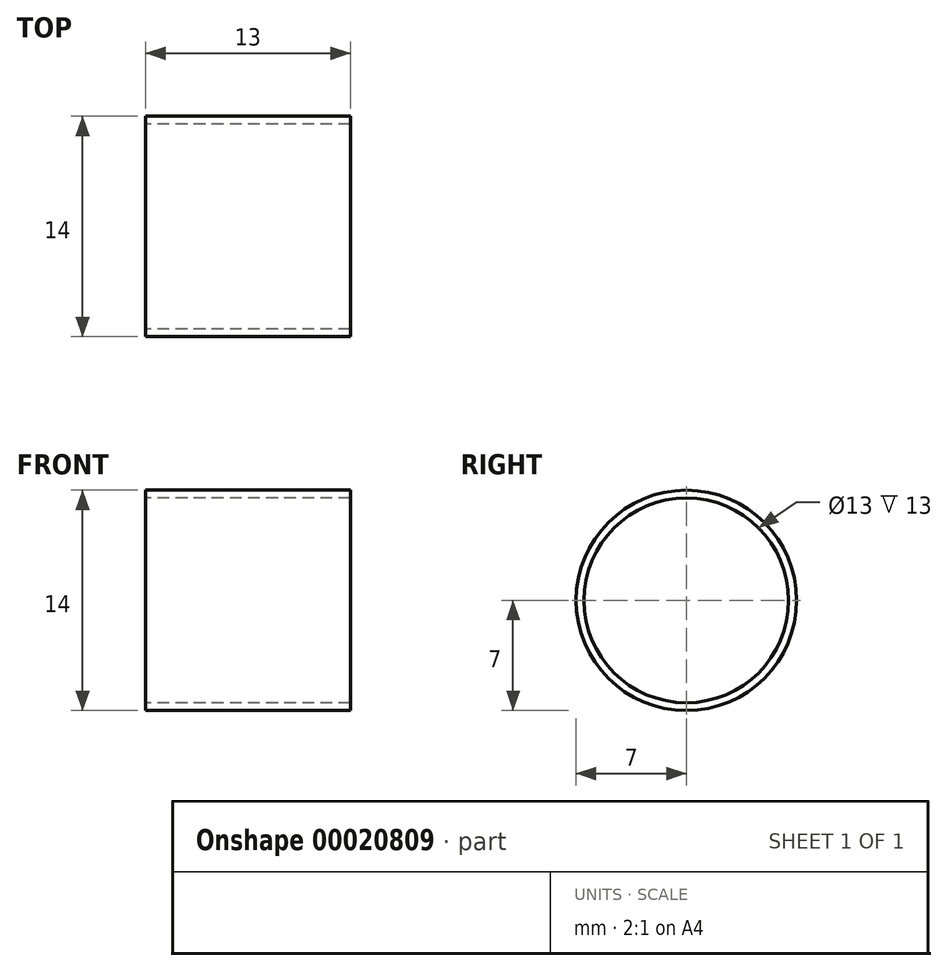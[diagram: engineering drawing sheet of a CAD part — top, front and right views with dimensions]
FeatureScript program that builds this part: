
annotation { "Feature Type Name" : "Feature", "Feature Type Description" : "" }
export const myFeature = defineFeature(function(context is Context, id is Id, definition is map)
    precondition{}
    {
        {
            var Q0;
            Q0=qCreatedBy(makeId("Right.planeOp"),FACE);
            var sketch = newSketch(context, id + "F0", { "sketchPlane" : qUnion([Q0])});
            skCircle(sketch, "E0", {"center": v(0, 0) * mm, "radius": 7 * mm});
            skCircle(sketch, "E1", {"center": v(0, 0) * mm, "radius": 6.5 * mm});
            skSolve(sketch);
        }
        {
            var Q0;
            Q0=makeQuery(id+"F0.imprint","IMPRINT",FACE,{"disambiguationData":[TD([[makeQuery(id+"F0.imprint","IMPRINT",EDGE,{"derivedFrom":sQuery(id+"F0.wireOp",EDGE,"E0")}),1.0]])]});
            extrude(context, id + "F1", {"entities" : qUnion([Q0]), "depth" : 13 * mm});
        }
    });
